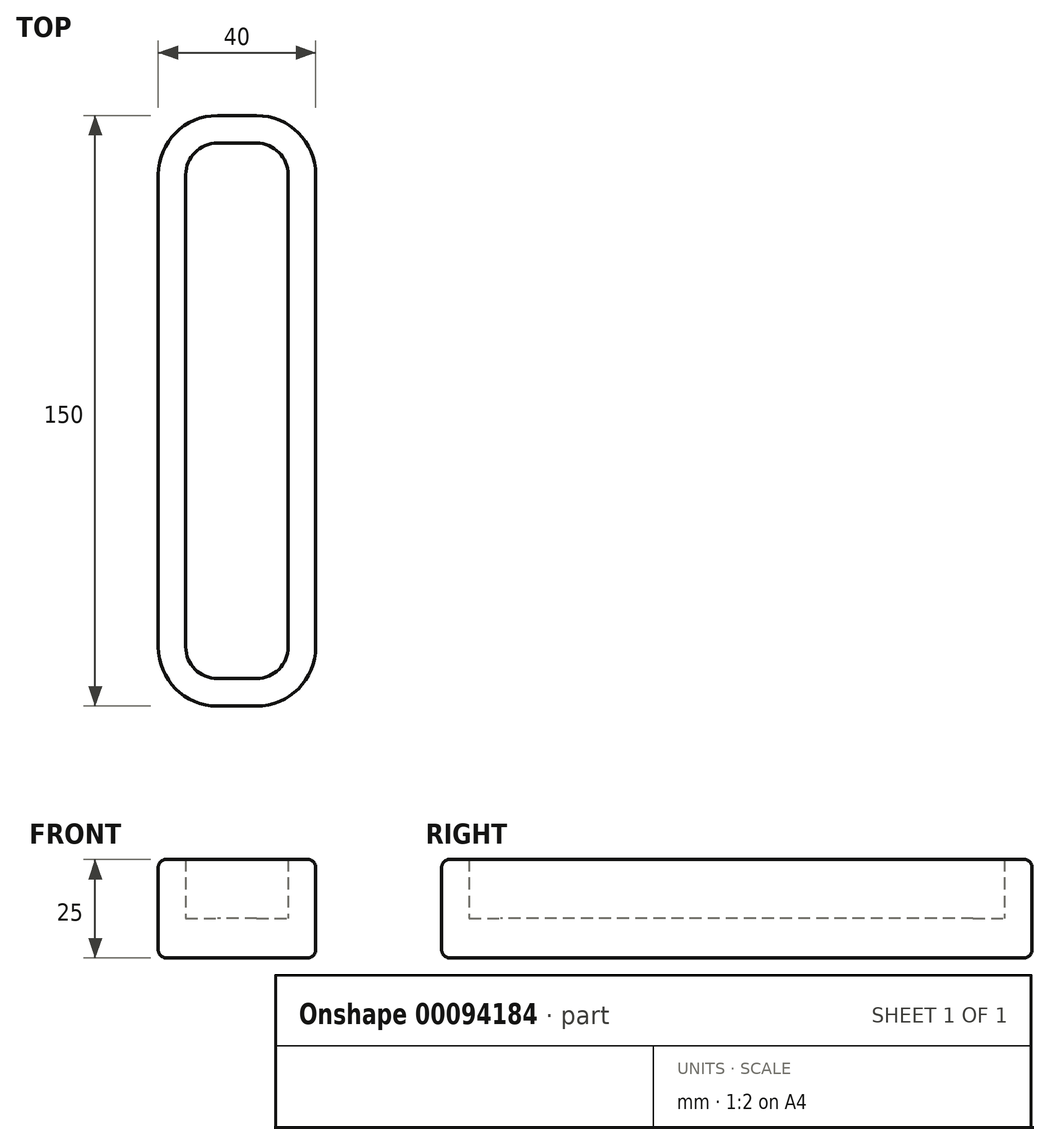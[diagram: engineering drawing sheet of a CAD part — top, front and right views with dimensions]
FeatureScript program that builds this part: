
annotation { "Feature Type Name" : "Feature", "Feature Type Description" : "" }
export const myFeature = defineFeature(function(context is Context, id is Id, definition is map)
    precondition{}
    {
        {
            var Q0;
            Q0=qCreatedBy(makeId("Top.planeOp"),FACE);
            var sketch = newSketch(context, id + "F0", { "sketchPlane" : qUnion([Q0])});
            skLineSegment(sketch, "E0.bottom", {"start": v(20, 75) * mm, "end": v(-20, 75) * mm});
            skLineSegment(sketch, "E0.top", {"start": v(20, -75) * mm, "end": v(-20, -75) * mm});
            skLineSegment(sketch, "E0.left", {"start": v(20, 75) * mm, "end": v(20, -75) * mm});
            skLineSegment(sketch, "E0.right", {"start": v(-20, 75) * mm, "end": v(-20, -75) * mm});
            skPoint(sketch, "E0.middle", {"position": v(0, 0) * mm});
            skSolve(sketch);
        }
        {
            var Q0;
            Q0=makeQuery(id+"F0.imprint","IMPRINT",FACE,{"disambiguationData":[TD([[makeQuery(id+"F0.imprint","IMPRINT",EDGE,{"derivedFrom":sQuery(id+"F0.wireOp",EDGE,"E0.bottom")}),1.0]])]});
            extrude(context, id + "F11", {"entities" : qUnion([Q0]), "depth" : 25 * mm});
        }
        {
            var Q0;
            Q0=makeQuery(id+"F11.opExtrude","SWEPT_EDGE",EDGE,{"disambiguationData":[OSD([sQuery(id+"F0.wireOp",EDGE,"E0.top"),sQuery(id+"F0.wireOp",EDGE,"E0.left")])]});
            fillet(context, id + "F1", {"entities" : qUnion([Q0]), "radius" : 15 * mm, "tangentPropagation" : true, "allowEdgeOverflow" : false});
        }
        {
            var Q0;
            Q0=makeQuery(id+"F11.opExtrude","SWEPT_EDGE",EDGE,{"disambiguationData":[OSD([sQuery(id+"F0.wireOp",EDGE,"E0.top"),sQuery(id+"F0.wireOp",EDGE,"E0.right")])]});
            fillet(context, id + "F2", {"entities" : qUnion([Q0]), "radius" : 15 * mm, "tangentPropagation" : true, "allowEdgeOverflow" : false});
        }
        {
            var Q0;
            Q0=makeQuery(id+"F11.opExtrude","SWEPT_EDGE",EDGE,{"disambiguationData":[OSD([sQuery(id+"F0.wireOp",EDGE,"E0.bottom"),sQuery(id+"F0.wireOp",EDGE,"E0.right")])]});
            var Q1;
            Q1=makeQuery(id+"F11.opExtrude","SWEPT_EDGE",EDGE,{"disambiguationData":[OSD([sQuery(id+"F0.wireOp",EDGE,"E0.bottom"),sQuery(id+"F0.wireOp",EDGE,"E0.left")])]});
            fillet(context, id + "F3", {"entities" : qUnion([Q0, Q1]), "radius" : 15 * mm, "tangentPropagation" : true, "allowEdgeOverflow" : false});
        }
        {
            var Q0;
            Q0=makeQuery(id+"F11.opExtrude","CAP_EDGE",EDGE,{"disambiguationData":[OSD([sQuery(id+"F0.wireOp",EDGE,"E0.left")])],"isStart":false});
            var Q1;
            Q1=makeQuery(id+"F11.opExtrude","CAP_EDGE",EDGE,{"disambiguationData":[OSD([sQuery(id+"F0.wireOp",EDGE,"E0.left")])],"isStart":true});
            fillet(context, id + "F4", {"entities" : qUnion([Q0, Q1]), "radius" : 2 * mm, "tangentPropagation" : true, "allowEdgeOverflow" : false});
        }
        {
            var Q0;
            Q0=makeQuery(id+"F11.opExtrude","CAP_FACE",FACE,{"disambiguationData":[OSD([sQuery(id+"F0.wireOp",EDGE,"E0.bottom"),sQuery(id+"F0.wireOp",EDGE,"E0.top"),sQuery(id+"F0.wireOp",EDGE,"E0.left"),sQuery(id+"F0.wireOp",EDGE,"E0.right")])],"isStart":false});
            shell(context, id + "F5", {"entities" : qUnion([Q0]), "thickness" : 7 * mm});
        }
        {
            var Q0;
            Q0=makeQuery(id+"F0.imprint","IMPRINT",FACE,{"disambiguationData":[TD([[makeQuery(id+"F0.imprint","IMPRINT",EDGE,{"derivedFrom":sQuery(id+"F0.wireOp",EDGE,"E0.bottom")}),1.0]])]});
            extrude(context, id + "F6", {"entities" : qUnion([Q0]), "operationType" : NewBodyOperationType.ADD, "depth" : 10 * mm});
        }
        {
            var Q0;
            Q0=makeQuery(id+"F6.opExtrude","SWEPT_EDGE",EDGE,{"disambiguationData":[OSD([sQuery(id+"F0.wireOp",EDGE,"E0.top"),sQuery(id+"F0.wireOp",EDGE,"E0.left")])]});
            var Q1;
            Q1=makeQuery(id+"F6.opExtrude","SWEPT_EDGE",EDGE,{"disambiguationData":[OSD([sQuery(id+"F0.wireOp",EDGE,"E0.top"),sQuery(id+"F0.wireOp",EDGE,"E0.right")])]});
            var Q2;
            Q2=makeQuery(id+"F6.opExtrude","SWEPT_EDGE",EDGE,{"disambiguationData":[OSD([sQuery(id+"F0.wireOp",EDGE,"E0.bottom"),sQuery(id+"F0.wireOp",EDGE,"E0.left")])]});
            var Q3;
            Q3=makeQuery(id+"F6.opExtrude","SWEPT_EDGE",EDGE,{"disambiguationData":[OSD([sQuery(id+"F0.wireOp",EDGE,"E0.bottom"),sQuery(id+"F0.wireOp",EDGE,"E0.right")])]});
            fillet(context, id + "F12", {"entities" : qUnion([Q0, Q1, Q2, Q3]), "radius" : 15 * mm, "tangentPropagation" : true, "allowEdgeOverflow" : false});
        }
        {
            var Q0;
            Q0=makeQuery(id+"F6.opExtrude","CAP_EDGE",EDGE,{"disambiguationData":[OSD([sQuery(id+"F0.wireOp",EDGE,"E0.left")])],"isStart":true});
            fillet(context, id + "F7", {"entities" : qUnion([Q0]), "radius" : 2 * mm, "tangentPropagation" : true, "allowEdgeOverflow" : false});
        }
    });
